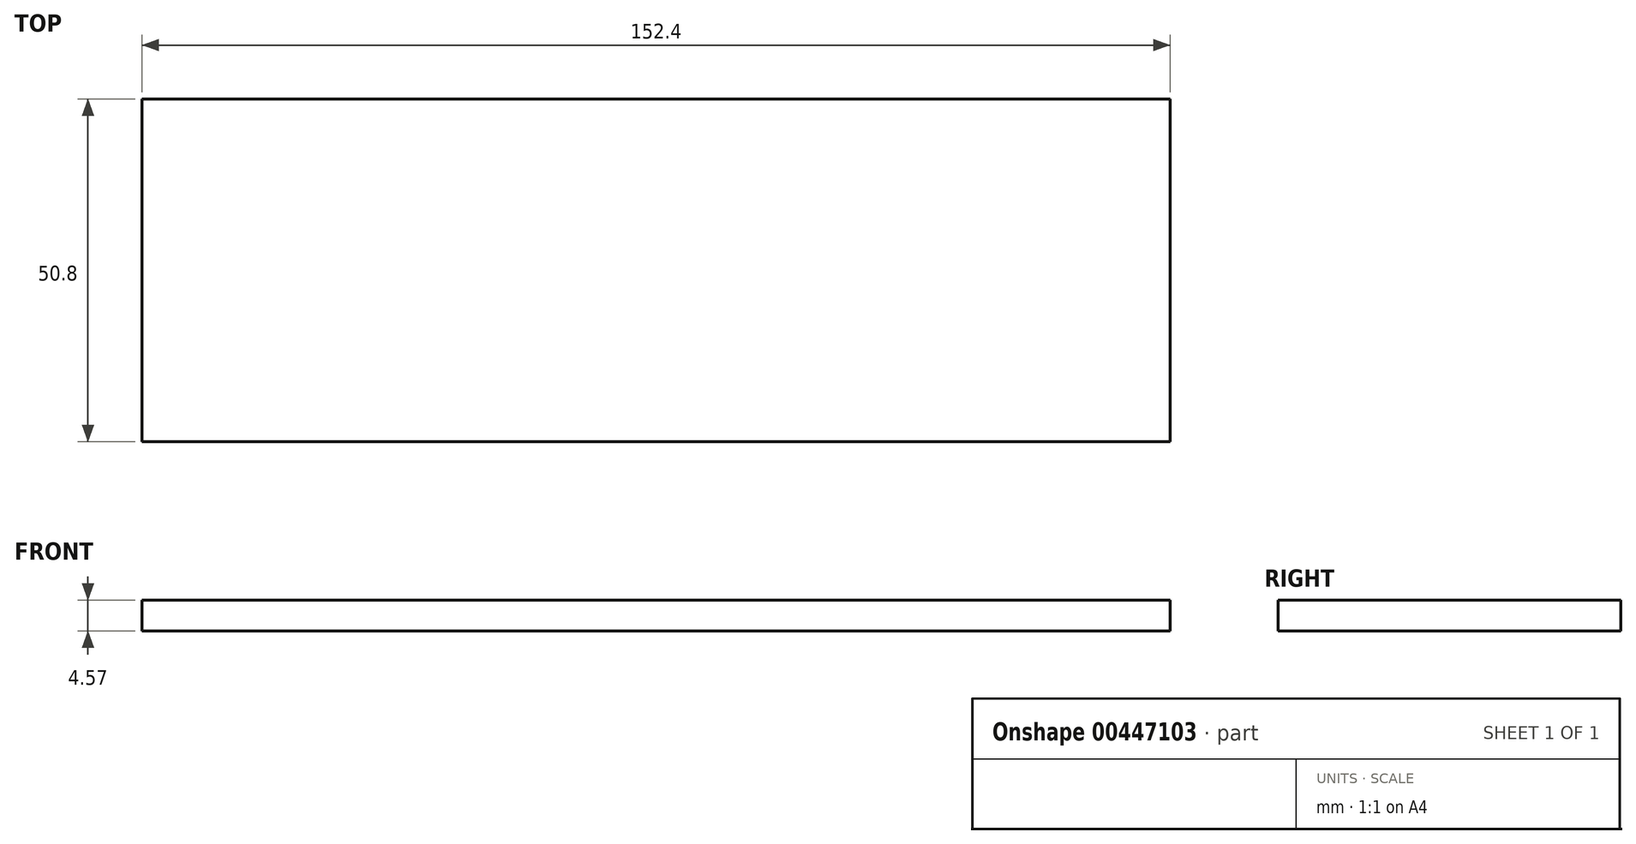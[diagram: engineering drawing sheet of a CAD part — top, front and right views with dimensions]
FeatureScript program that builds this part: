
annotation { "Feature Type Name" : "Feature", "Feature Type Description" : "" }
export const myFeature = defineFeature(function(context is Context, id is Id, definition is map)
    precondition{}
    {
        {
            var Q0;
            Q0=qCreatedBy(makeId("Top.planeOp"),FACE);
            var sketch = newSketch(context, id + "F0", { "sketchPlane" : qUnion([Q0])});
            skLineSegment(sketch, "E0.bottom", {"start": v(-75.97, 28.54) * mm, "end": v(76.43, 28.54) * mm});
            skLineSegment(sketch, "E0.top", {"start": v(-75.97, -22.26) * mm, "end": v(76.43, -22.26) * mm});
            skLineSegment(sketch, "E0.left", {"start": v(-75.97, 28.54) * mm, "end": v(-75.97, -22.26) * mm});
            skLineSegment(sketch, "E0.right", {"start": v(76.43, 28.54) * mm, "end": v(76.43, -22.26) * mm});
            skSolve(sketch);
        }
        {
            var Q0;
            Q0=sQuery(id+"F0.wireOp",EDGE,"E0.right");
            var Q1;
            Q1=sQuery(id+"F0.wireOp",EDGE,"E0.top");
            var Q2;
            Q2=sQuery(id+"F0.wireOp",EDGE,"E0.bottom");
            var Q3;
            Q3=sQuery(id+"F0.wireOp",EDGE,"E0.left");
            extrude(context, id + "F1", {"bodyType" : ToolBodyType.SURFACE, "surfaceEntities" : qUnion([Q0, Q1, Q2, Q3]), "depth" : 4.57 * mm});
        }
    });
